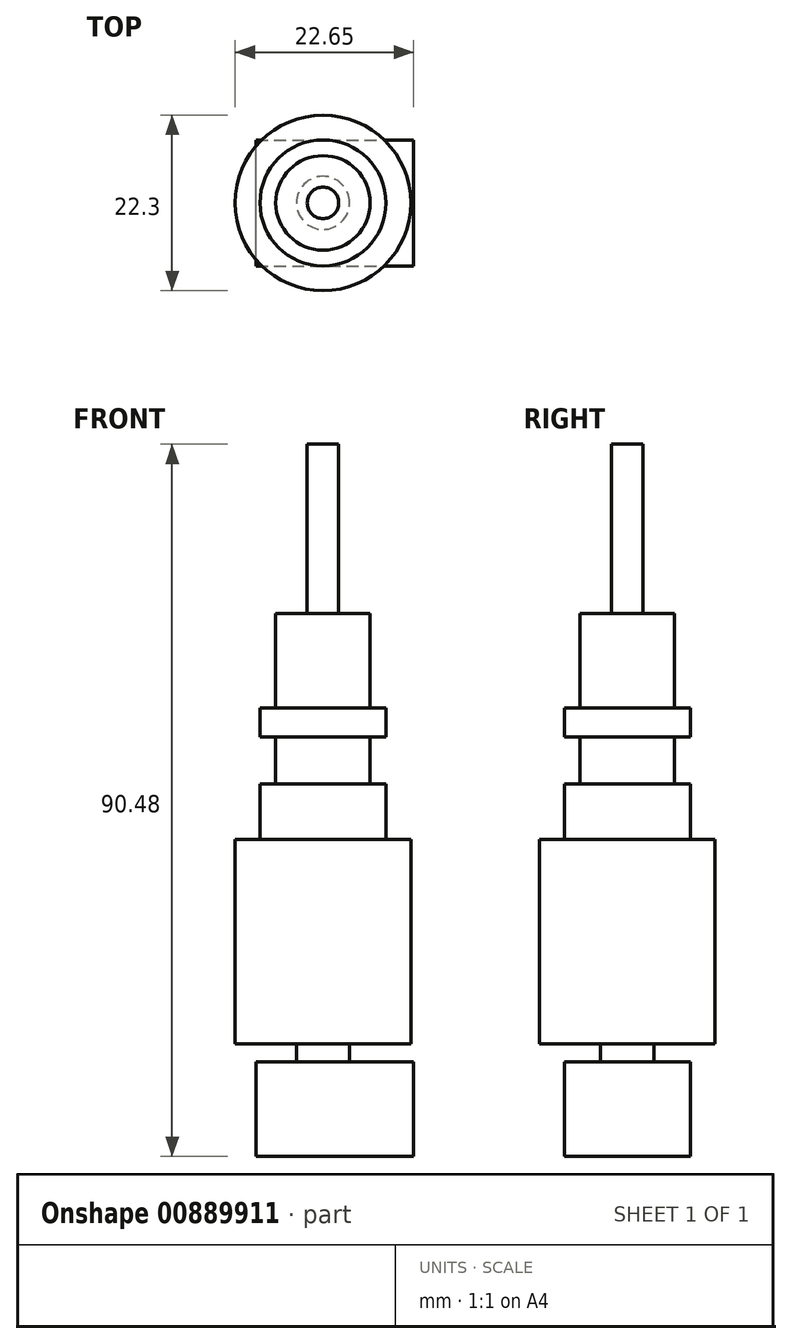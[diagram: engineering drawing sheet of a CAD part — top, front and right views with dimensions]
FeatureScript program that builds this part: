
annotation { "Feature Type Name" : "Feature", "Feature Type Description" : "" }
export const myFeature = defineFeature(function(context is Context, id is Id, definition is map)
    precondition{}
    {
        {
            var Q0;
            Q0=qCreatedBy(makeId("Front.planeOp"),FACE);
            var sketch = newSketch(context, id + "F0", { "sketchPlane" : qUnion([Q0])});
            skLineSegment(sketch, "E0", {"start": v(0, 0) * mm, "end": v(-3.38, 0) * mm});
            skLineSegment(sketch, "E1", {"start": v(-3.38, 0) * mm, "end": v(-3.38, 2.3) * mm});
            skLineSegment(sketch, "E2", {"start": v(-3.37, 2.3) * mm, "end": v(-11.15, 2.3) * mm});
            skLineSegment(sketch, "E3", {"start": v(-11.15, 2.3) * mm, "end": v(-11.15, 28.3) * mm});
            skLineSegment(sketch, "E4", {"start": v(-11.15, 28.3) * mm, "end": v(-8, 28.3) * mm});
            skLineSegment(sketch, "E5", {"start": v(-8, 28.3) * mm, "end": v(-8, 35.3) * mm});
            skLineSegment(sketch, "E6", {"start": v(-8, 35.3) * mm, "end": v(-6, 35.3) * mm});
            skLineSegment(sketch, "E7", {"start": v(-6, 35.3) * mm, "end": v(-6, 41.3) * mm});
            skLineSegment(sketch, "E8", {"start": v(-6, 41.3) * mm, "end": v(-8, 41.3) * mm});
            skLineSegment(sketch, "E9", {"start": v(-8, 41.3) * mm, "end": v(-8, 45) * mm});
            skLineSegment(sketch, "E10", {"start": v(-8, 45) * mm, "end": v(-6, 45) * mm});
            skLineSegment(sketch, "E11", {"start": v(-6, 45) * mm, "end": v(-6, 57) * mm});
            skLineSegment(sketch, "E12", {"start": v(-6, 57) * mm, "end": v(-2, 57) * mm});
            skLineSegment(sketch, "E13", {"start": v(-2, 57) * mm, "end": v(-2, 78.48) * mm});
            skLineSegment(sketch, "E14", {"start": v(-2, 78.48) * mm, "end": v(0, 78.48) * mm});
            skLineSegment(sketch, "E15", {"start": v(0, 78.48) * mm, "end": v(0, 0) * mm});
            skLineSegment(sketch, "E16", {"start": v(0, -4.63) * mm, "end": v(0, 79.74) * mm, "construction": true});
            skSolve(sketch);
        }
        {
            var Q0;
            Q0 = qSketchRegion(id + "F0", true);
            var Q1;
            Q1=sQuery(id+"F0.wireOp",EDGE,"E16");
            revolve(context, id + "F1", {"surfaceOperationType" : NewSurfaceOperationType.NEW, "entities" : qUnion([Q0]), "axis" : qUnion([Q1]), "revolveType" : RevolveType.FULL});
        }
        {
            var Q0;
            Q0=qCreatedBy(makeId("Front.planeOp"),FACE);
            var sketch = newSketch(context, id + "F2", { "sketchPlane" : qUnion([Q0])});
            skLineSegment(sketch, "E17.bottom", {"start": v(-8.5, 0) * mm, "end": v(11.5, 0) * mm});
            skLineSegment(sketch, "E17.top", {"start": v(-8.5, -12) * mm, "end": v(11.5, -12) * mm});
            skLineSegment(sketch, "E17.left", {"start": v(-8.5, 0) * mm, "end": v(-8.5, -12) * mm});
            skLineSegment(sketch, "E17.right", {"start": v(11.5, 0) * mm, "end": v(11.5, -12) * mm});
            skSolve(sketch);
        }
        {
            var Q0;
            Q0 = qSketchRegion(id + "F2", true);
            extrude(context, id + "F3", {"entities" : qUnion([Q0]), "operationType" : NewBodyOperationType.ADD, "depth" : 16 * mm, "offsetDistance" : 25 * mm, "symmetric" : true});
        }
    });
